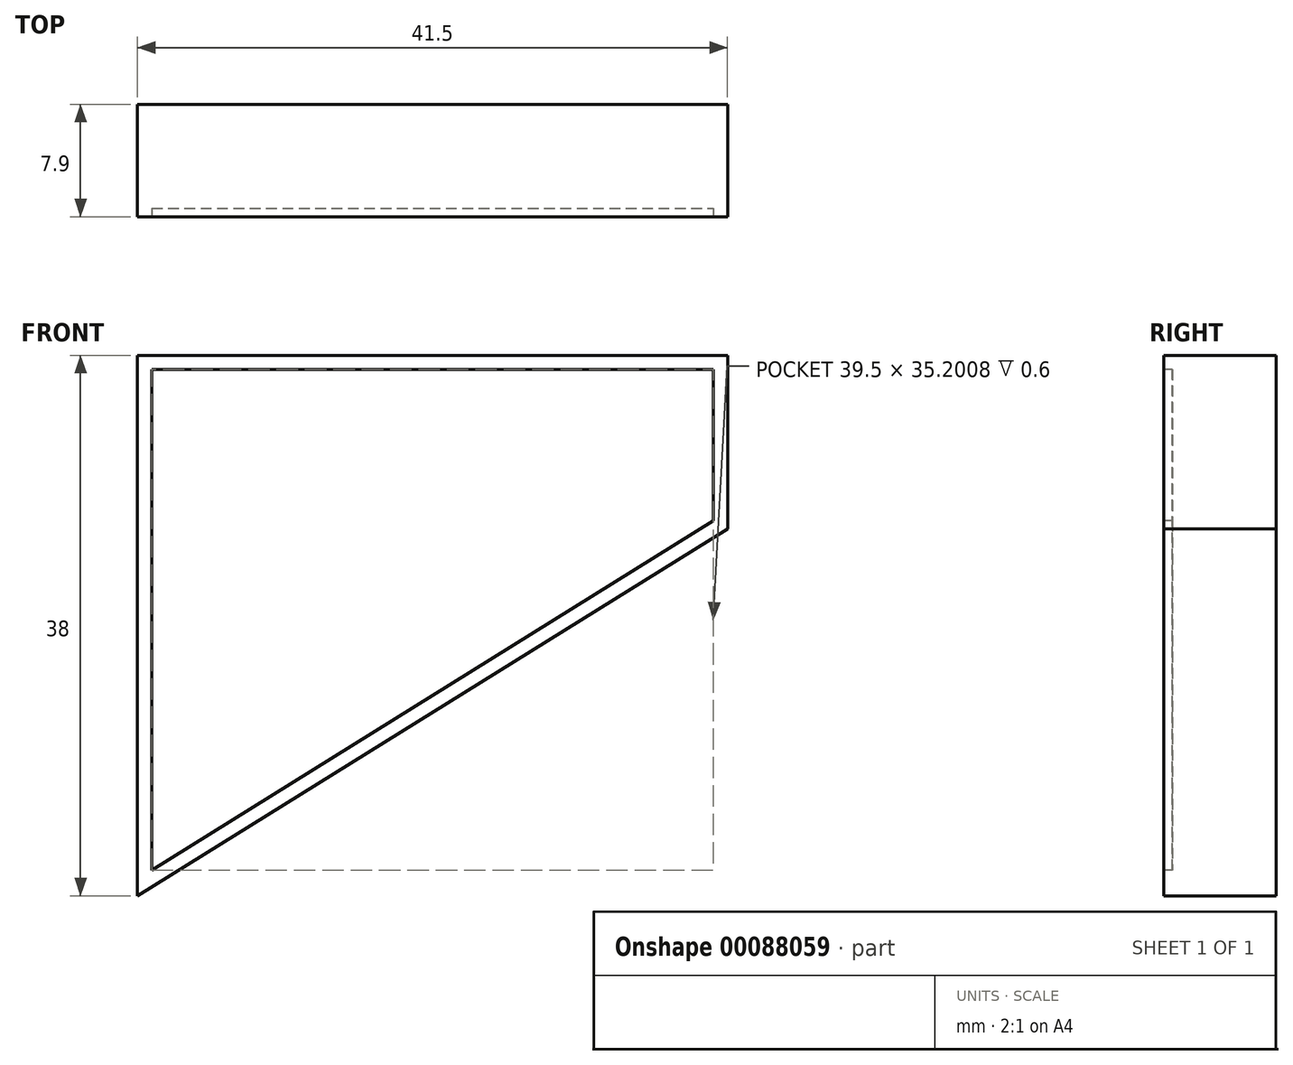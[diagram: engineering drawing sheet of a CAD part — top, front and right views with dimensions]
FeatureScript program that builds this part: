
annotation { "Feature Type Name" : "Feature", "Feature Type Description" : "" }
export const myFeature = defineFeature(function(context is Context, id is Id, definition is map)
    precondition{}
    {
        {
            var Q0;
            Q0=qCreatedBy(makeId("Front.planeOp"),FACE);
            var sketch = newSketch(context, id + "F0", { "sketchPlane" : qUnion([Q0])});
            skLineSegment(sketch, "E0", {"start": v(-32.34, -15.26) * mm, "end": v(-32.34, 22.74) * mm});
            skLineSegment(sketch, "E1", {"start": v(-32.34, 22.74) * mm, "end": v(9.16, 22.74) * mm});
            skLineSegment(sketch, "E2", {"start": v(9.16, 22.74) * mm, "end": v(9.16, 10.54) * mm});
            skLineSegment(sketch, "E3", {"start": v(9.16, 10.54) * mm, "end": v(-32.34, -15.26) * mm});
            skSolve(sketch);
        }
        {
            var Q0;
            Q0 = qSketchRegion(id + "F0", true);
            extrude(context, id + "F1", {"entities" : qUnion([Q0]), "depth" : 7.9 * mm, "offsetDistance" : 25 * mm});
        }
        {
            var Q0;
            Q0=makeQuery(id+"F1.opExtrude","CAP_FACE",FACE,{"disambiguationData":[OSD([sQuery(id+"F0.wireOp",EDGE,"E0"),sQuery(id+"F0.wireOp",EDGE,"E1"),sQuery(id+"F0.wireOp",EDGE,"E2"),sQuery(id+"F0.wireOp",EDGE,"E3")])],"isStart":false});
            var sketch = newSketch(context, id + "F2", { "sketchPlane" : qUnion([Q0])});
            skLineSegment(sketch, "E4.0", {"start": v(-31.34, 21.74) * mm, "end": v(8.16, 21.74) * mm});
            skLineSegment(sketch, "E4.1", {"start": v(-31.34, -13.46) * mm, "end": v(-31.34, 21.74) * mm});
            skLineSegment(sketch, "E4.2", {"start": v(8.16, 11.1) * mm, "end": v(-31.34, -13.46) * mm});
            skLineSegment(sketch, "E4.3", {"start": v(8.16, 21.74) * mm, "end": v(8.16, 11.1) * mm});
            skSolve(sketch);
        }
        {
            var Q0;
            Q0 = qSketchRegion(id + "F2", true);
            extrude(context, id + "F3", {"entities" : qUnion([Q0]), "operationType" : NewBodyOperationType.REMOVE, "oppositeDirection" : true, "depth" : .6 * mm, "offsetDistance" : 25 * mm});
        }
    });
